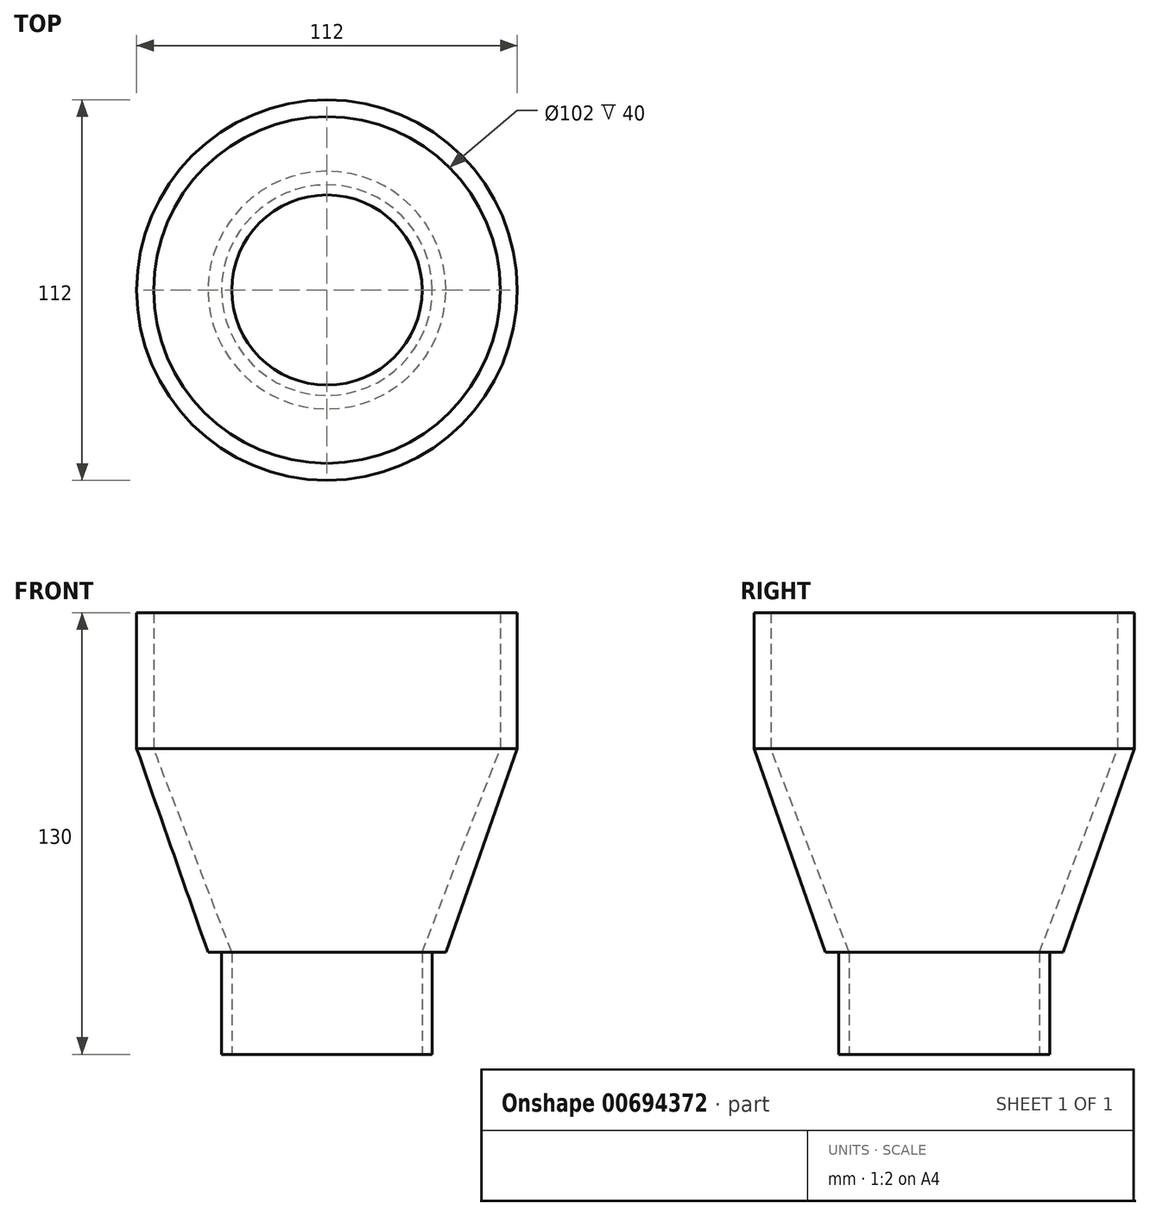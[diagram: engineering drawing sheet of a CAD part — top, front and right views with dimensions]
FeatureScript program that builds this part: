
annotation { "Feature Type Name" : "Feature", "Feature Type Description" : "" }
export const myFeature = defineFeature(function(context is Context, id is Id, definition is map)
    precondition{}
    {
        {
            var Q0;
            Q0=qCreatedBy(makeId("Front.planeOp"),FACE);
            var sketch = newSketch(context, id + "F0", { "sketchPlane" : qUnion([Q0])});
            skLineSegment(sketch, "E0", {"start": v(-3, 0) * mm, "end": v(-3, 30) * mm});
            skLineSegment(sketch, "E1", {"start": v(0, 30) * mm, "end": v(-23, 90) * mm});
            skLineSegment(sketch, "E2", {"start": v(-23, 90) * mm, "end": v(-23, 130) * mm});
            skLineSegment(sketch, "E3", {"start": v(-28, 90) * mm, "end": v(-28, 130) * mm});
            skLineSegment(sketch, "E4", {"start": v(-28, 130) * mm, "end": v(-23, 130) * mm});
            skLineSegment(sketch, "E5", {"start": v(28, 0) * mm, "end": v(28, 7.26) * mm});
            skLineSegment(sketch, "E6", {"start": v(0, 0) * mm, "end": v(0, 30) * mm});
            skLineSegment(sketch, "E7", {"start": v(-3, 0) * mm, "end": v(0, 0) * mm});
            skLineSegment(sketch, "E8", {"start": v(-3, 30) * mm, "end": v(-7, 30) * mm});
            skLineSegment(sketch, "E9", {"start": v(-7, 30) * mm, "end": v(-28, 90) * mm});
            skSolve(sketch);
        }
        {
            var Q0;
            Q0=makeQuery(id+"F0.imprint","IMPRINT",FACE,{"disambiguationData":[TD([[makeQuery(id+"F0.imprint","IMPRINT",EDGE,{"derivedFrom":sQuery(id+"F0.wireOp",EDGE,"E0")}),-1.0]])]});
            var Q1;
            Q1=sQuery(id+"F0.wireOp",EDGE,"E5");
            revolve(context, id + "F1", {"surfaceOperationType" : NewSurfaceOperationType.NEW, "entities" : qUnion([Q0]), "axis" : qUnion([Q1]), "revolveType" : RevolveType.FULL});
        }
    });
